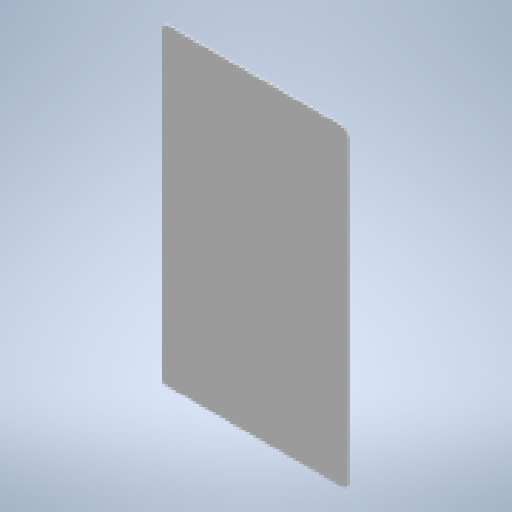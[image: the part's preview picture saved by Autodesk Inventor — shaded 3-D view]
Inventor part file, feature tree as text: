
AUTODESK INVENTOR PART (.ipt)
format: ipt  version: 2025 (Build 290162000, 162)  size: 135,680 bytes
history: native  units: mm
features: reference x9, extrude x1, sketch x1, other x1
ambient origin geometry x8: Origin, YZ Plane, XZ Plane, XY Plane, X Axis, Y Axis, Z Axis, Center Point
bodies: Solid1 (feature_tree)
feature tree (12):
  extrude  "Extrusion1"  Depth=0.2mm TaperAngle=0.0deg
  sketch  "Sketch1"  dims[d0=40.99mm d1=0.2mm d2=0.0mm]
  reference  "Reference1"
  reference  "Reference2"
  reference  "Reference3"
  reference  "Reference4"
  reference  "Reference5"
  reference  "Reference6"
  reference  "Reference7"
  reference  "Reference8"
  reference  "Reference9"
  other  "tamale_flex.iam"
